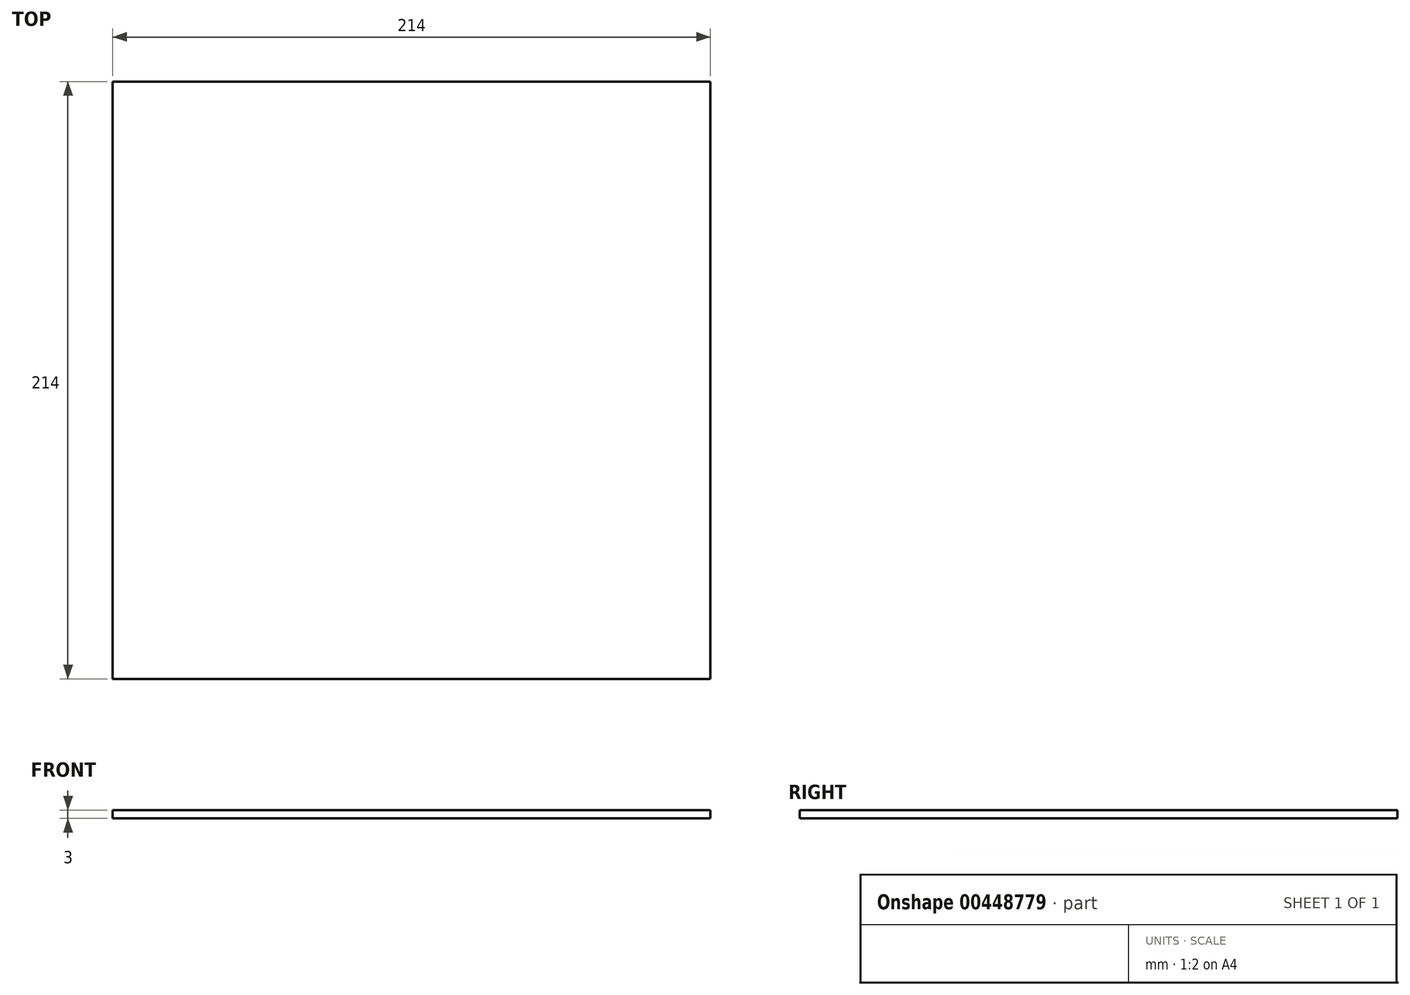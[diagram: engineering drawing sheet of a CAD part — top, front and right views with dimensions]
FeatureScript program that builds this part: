
annotation { "Feature Type Name" : "Feature", "Feature Type Description" : "" }
export const myFeature = defineFeature(function(context is Context, id is Id, definition is map)
    precondition{}
    {
        {
            var Q0;
            Q0=qCreatedBy(makeId("Top.planeOp"),FACE);
            var sketch = newSketch(context, id + "F0", { "sketchPlane" : qUnion([Q0])});
            skLineSegment(sketch, "E0.bottom", {"start": v(0, 0) * mm, "end": v(214, 0) * mm});
            skLineSegment(sketch, "E0.top", {"start": v(0, 214) * mm, "end": v(214, 214) * mm});
            skLineSegment(sketch, "E0.left", {"start": v(0, 0) * mm, "end": v(0, 214) * mm});
            skLineSegment(sketch, "E0.right", {"start": v(214, 0) * mm, "end": v(214, 214) * mm});
            skSolve(sketch);
        }
        {
            var Q0;
            Q0=makeQuery(id+"F0.imprint","IMPRINT",FACE,{"disambiguationData":[TD([[makeQuery(id+"F0.imprint","IMPRINT",EDGE,{"derivedFrom":sQuery(id+"F0.wireOp",EDGE,"E0.bottom")}),1.0]])]});
            extrude(context, id + "F1", {"entities" : qUnion([Q0]), "depth" : 3 * mm});
        }
    });
